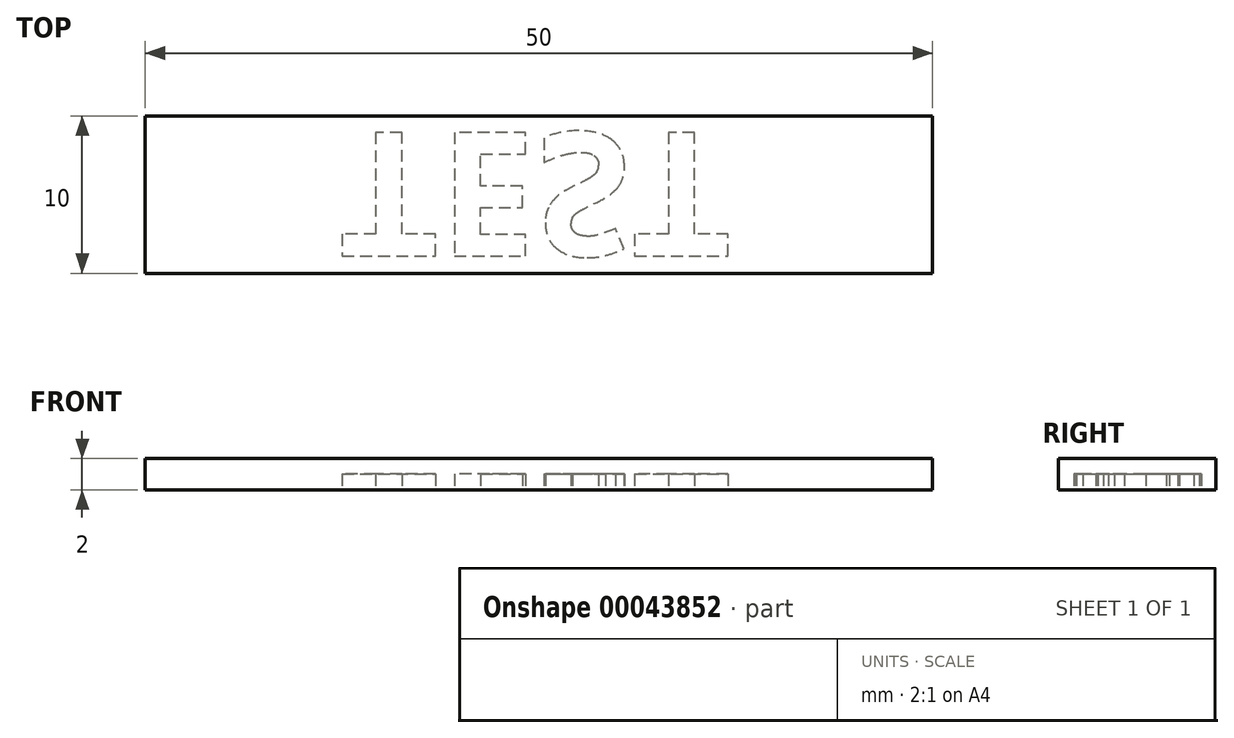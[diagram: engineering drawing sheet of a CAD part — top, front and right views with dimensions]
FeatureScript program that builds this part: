
annotation { "Feature Type Name" : "Feature", "Feature Type Description" : "" }
export const myFeature = defineFeature(function(context is Context, id is Id, definition is map)
    precondition{}
    {
        {
            var Q0;
            Q0=qCreatedBy(makeId("Top.planeOp"),FACE);
            var sketch = newSketch(context, id + "F0", { "sketchPlane" : qUnion([Q0])});
            skLineSegment(sketch, "E0.bottom", {"start": v(25, -5) * mm, "end": v(-25, -5) * mm});
            skLineSegment(sketch, "E0.top", {"start": v(25, 5) * mm, "end": v(-25, 5) * mm});
            skLineSegment(sketch, "E0.left", {"start": v(25, -5) * mm, "end": v(25, 5) * mm});
            skLineSegment(sketch, "E0.right", {"start": v(-25, -5) * mm, "end": v(-25, 5) * mm});
            skPoint(sketch, "E0.middle", {"position": v(0, 0) * mm});
            skSolve(sketch);
        }
        {
            var Q0;
            Q0 = qSketchRegion(id + "F0", true);
            extrude(context, id + "F1", {"entities" : qUnion([Q0]), "depth" : 2 * mm});
        }
        {
            var Q0;
            Q0=makeQuery(id+"F1.opExtrude","CAP_FACE",FACE,{"disambiguationData":[OSD([sQuery(id+"F0.wireOp",EDGE,"E0.bottom"),sQuery(id+"F0.wireOp",EDGE,"E0.top"),sQuery(id+"F0.wireOp",EDGE,"E0.left"),sQuery(id+"F0.wireOp",EDGE,"E0.right")])],"isStart":true});
            var sketch = newSketch(context, id + "F2", { "sketchPlane" : qUnion([Q0])});
            skText(sketch, "E1", { "text": "TEST", "fontName": "OpenSans-Bold.ttf"});
            skLineSegment(sketch, "E2", {"start": v(12.72, 0) * mm, "end": v(25, 0) * mm, "construction": true});
            skLineSegment(sketch, "E3", {"start": v(-25, 0) * mm, "end": v(-12.72, 0) * mm, "construction": true});
            const initialGuessF2  = {"E1": [-0.01272, -0.00396, 1, 0, 0.00792]};
            skSetInitialGuess(sketch, initialGuessF2);
            skSolve(sketch);
        }
        {
            var Q0;
            Q0 = qSketchRegion(id + "F2", true);
            extrude(context, id + "F3", {"entities" : qUnion([Q0]), "operationType" : NewBodyOperationType.REMOVE, "oppositeDirection" : true, "depth" : 1 * mm});
        }
    });
